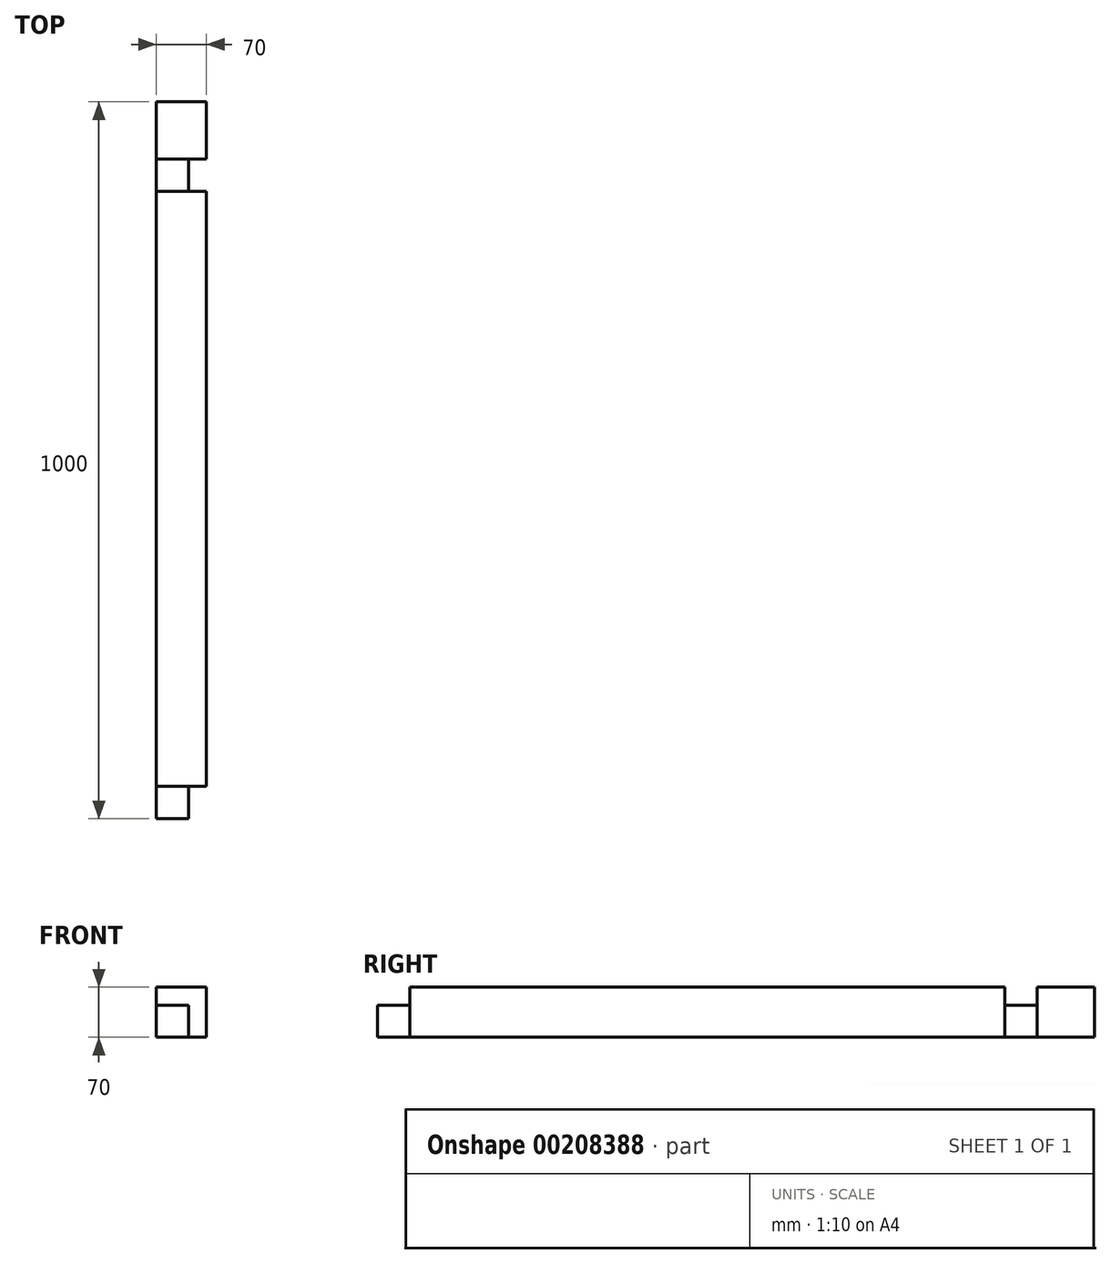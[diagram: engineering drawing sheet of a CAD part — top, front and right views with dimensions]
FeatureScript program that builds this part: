
annotation { "Feature Type Name" : "Feature", "Feature Type Description" : "" }
export const myFeature = defineFeature(function(context is Context, id is Id, definition is map)
    precondition{}
    {
        {
            var Q0;
            Q0=qCreatedBy(makeId("Front.planeOp"),FACE);
            var sketch = newSketch(context, id + "F0", { "sketchPlane" : qUnion([Q0])});
            skLineSegment(sketch, "E0.bottom", {"start": v(-35, 35) * mm, "end": v(35, 35) * mm});
            skLineSegment(sketch, "E0.top", {"start": v(-35, -35) * mm, "end": v(35, -35) * mm});
            skLineSegment(sketch, "E0.left", {"start": v(-35, 35) * mm, "end": v(-35, -35) * mm});
            skLineSegment(sketch, "E0.right", {"start": v(35, 35) * mm, "end": v(35, -35) * mm});
            skSolve(sketch);
        }
        {
            var Q0;
            Q0=makeQuery(id+"F0.imprint","IMPRINT",FACE,{"disambiguationData":[TD([[makeQuery(id+"F0.imprint","IMPRINT",EDGE,{"derivedFrom":sQuery(id+"F0.wireOp",EDGE,"E0.bottom")}),-1.0]])]});
            extrude(context, id + "F1", {"entities" : qUnion([Q0]), "oppositeDirection" : true, "depth" : 1000 * mm});
        }
        {
            var Q0;
            Q0=makeQuery(id+"F1.opExtrude","SWEPT_FACE",FACE,{"disambiguationData":[OSD([sQuery(id+"F0.wireOp",EDGE,"E0.bottom")])]});
            var sketch = newSketch(context, id + "F2", { "sketchPlane" : qUnion([Q0])});
            skLineSegment(sketch, "E1.bottom", {"start": v(-35, 45) * mm, "end": v(35, 45) * mm});
            skLineSegment(sketch, "E1.top", {"start": v(-35, 0) * mm, "end": v(35, 0) * mm});
            skLineSegment(sketch, "E1.left", {"start": v(-35, 45) * mm, "end": v(-35, 0) * mm});
            skLineSegment(sketch, "E1.right", {"start": v(35, 45) * mm, "end": v(35, 0) * mm});
            skSolve(sketch);
        }
        {
            var Q0;
            Q0=makeQuery(id+"F2.imprint","IMPRINT",FACE,{"disambiguationData":[TD([[makeQuery(id+"F2.imprint","IMPRINT",EDGE,{"derivedFrom":sQuery(id+"F2.wireOp",EDGE,"E1.bottom")}),-1.0]])]});
            extrude(context, id + "F3", {"entities" : qUnion([Q0]), "operationType" : NewBodyOperationType.REMOVE, "oppositeDirection" : true, "depth" : 25 * mm});
        }
        {
            var Q0;
            Q0=makeQuery(id+"F1.opExtrude","SWEPT_FACE",FACE,{"disambiguationData":[OSD([sQuery(id+"F0.wireOp",EDGE,"E0.right")])]});
            var sketch = newSketch(context, id + "F4", { "sketchPlane" : qUnion([Q0])});
            skLineSegment(sketch, "E2.bottom", {"start": v(45, 10) * mm, "end": v(0, 10) * mm});
            skLineSegment(sketch, "E2.top", {"start": v(45, -35) * mm, "end": v(0, -35) * mm});
            skLineSegment(sketch, "E2.left", {"start": v(45, 10) * mm, "end": v(45, -35) * mm});
            skLineSegment(sketch, "E2.right", {"start": v(0, 10) * mm, "end": v(0, -35) * mm});
            skSolve(sketch);
        }
        {
            var Q0;
            Q0=makeQuery(id+"F4.imprint","IMPRINT",FACE,{"disambiguationData":[TD([[makeQuery(id+"F4.imprint","IMPRINT",EDGE,{"derivedFrom":sQuery(id+"F4.wireOp",EDGE,"E2.top")}),-1.0]])]});
            extrude(context, id + "F5", {"entities" : qUnion([Q0]), "operationType" : NewBodyOperationType.REMOVE, "oppositeDirection" : true, "depth" : 25 * mm});
        }
        {
            var Q0;
            Q0=makeQuery(id+"F1.opExtrude","SWEPT_FACE",FACE,{"disambiguationData":[OSD([sQuery(id+"F0.wireOp",EDGE,"E0.bottom")])]});
            var sketch = newSketch(context, id + "F6", { "sketchPlane" : qUnion([Q0])});
            skLineSegment(sketch, "E3.bottom", {"start": v(-35, 920) * mm, "end": v(35, 920) * mm});
            skLineSegment(sketch, "E3.top", {"start": v(-35, 875) * mm, "end": v(35, 875) * mm});
            skLineSegment(sketch, "E3.left", {"start": v(-35, 920) * mm, "end": v(-35, 875) * mm});
            skLineSegment(sketch, "E3.right", {"start": v(35, 920) * mm, "end": v(35, 875) * mm});
            skSolve(sketch);
        }
        {
            var Q0;
            Q0=makeQuery(id+"F6.imprint","IMPRINT",FACE,{"disambiguationData":[TD([[makeQuery(id+"F6.imprint","IMPRINT",EDGE,{"derivedFrom":sQuery(id+"F6.wireOp",EDGE,"E3.bottom")}),-1.0]])]});
            extrude(context, id + "F7", {"entities" : qUnion([Q0]), "operationType" : NewBodyOperationType.REMOVE, "oppositeDirection" : true, "depth" : 25 * mm});
        }
        {
            var Q0;
            Q0=makeQuery(id+"F1.opExtrude","SWEPT_FACE",FACE,{"disambiguationData":[OSD([sQuery(id+"F0.wireOp",EDGE,"E0.right")])]});
            var sketch = newSketch(context, id + "F8", { "sketchPlane" : qUnion([Q0])});
            skLineSegment(sketch, "E4.bottom", {"start": v(920, 10) * mm, "end": v(875, 10) * mm});
            skLineSegment(sketch, "E4.top", {"start": v(920, -35) * mm, "end": v(875, -35) * mm});
            skLineSegment(sketch, "E4.left", {"start": v(920, 10) * mm, "end": v(920, -35) * mm});
            skLineSegment(sketch, "E4.right", {"start": v(875, 10) * mm, "end": v(875, -35) * mm});
            skSolve(sketch);
        }
        {
            var Q0;
            Q0=makeQuery(id+"F8.imprint","IMPRINT",FACE,{"disambiguationData":[TD([[makeQuery(id+"F8.imprint","IMPRINT",EDGE,{"derivedFrom":sQuery(id+"F8.wireOp",EDGE,"E4.bottom")}),1.0]])]});
            extrude(context, id + "F9", {"entities" : qUnion([Q0]), "operationType" : NewBodyOperationType.REMOVE, "oppositeDirection" : true, "depth" : 25 * mm});
        }
    });
